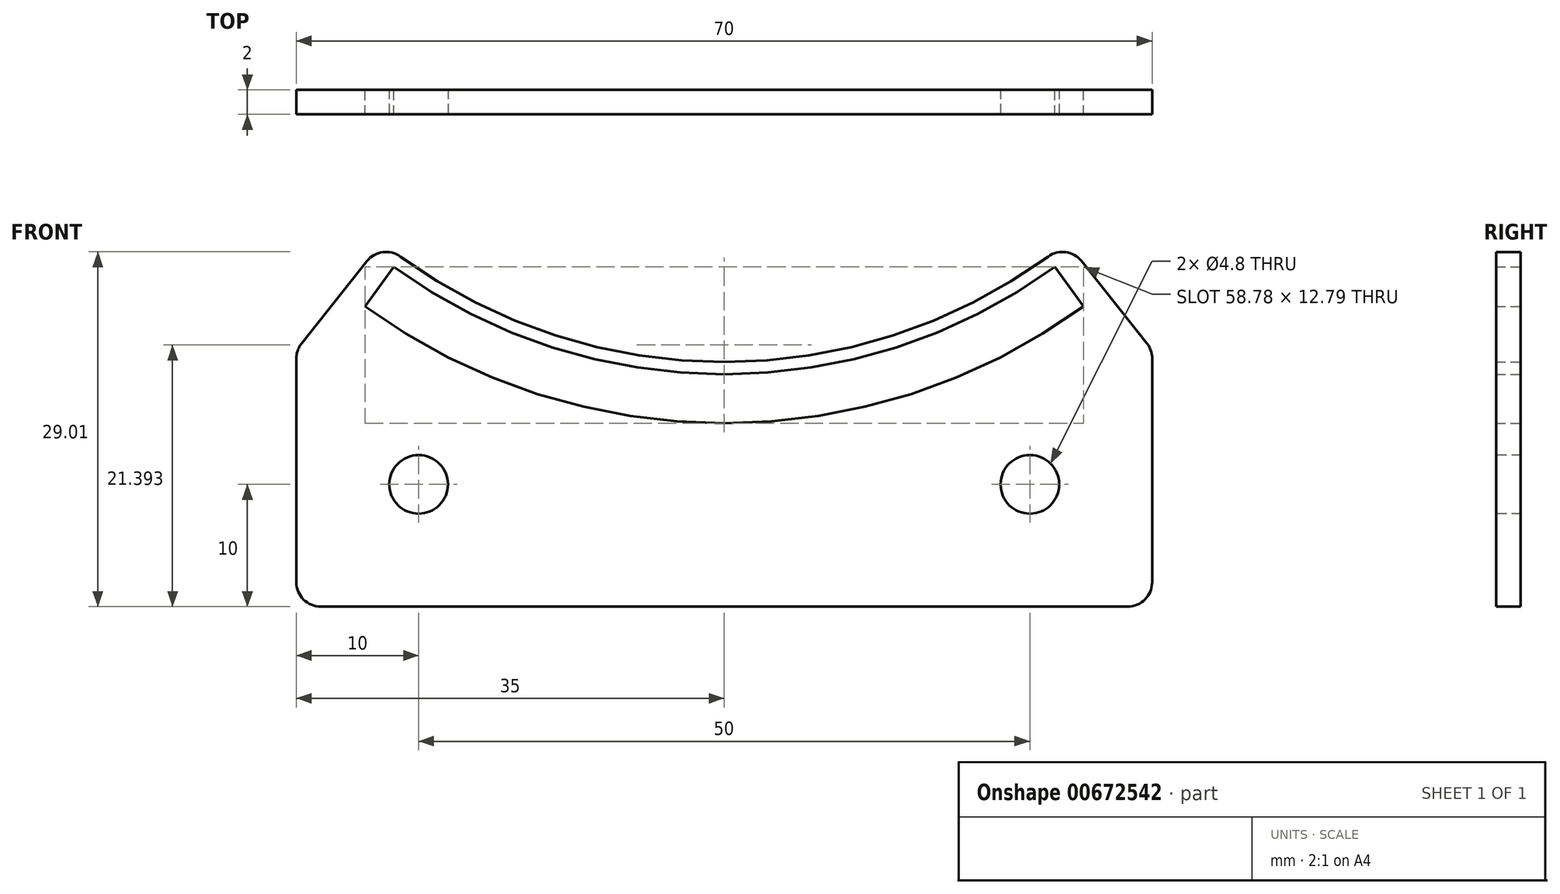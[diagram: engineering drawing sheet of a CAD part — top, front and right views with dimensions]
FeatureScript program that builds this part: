
annotation { "Feature Type Name" : "Feature", "Feature Type Description" : "" }
export const myFeature = defineFeature(function(context is Context, id is Id, definition is map)
    precondition{}
    {
        {
            var Q0;
            Q0=qCreatedBy(makeId("Front.planeOp"),FACE);
            var sketch = newSketch(context, id + "F0", { "sketchPlane" : qUnion([Q0])});
            skArc(sketch, "E0", {"start": v(-29.39, -40.45) * mm, "mid": v(0, -50) * mm, "end": v(29.39, -40.45) * mm});
            skArc(sketch, "E1", {"start": v(-27.04, -37.21) * mm, "mid": v(0, -46) * mm, "end": v(27.04, -37.21) * mm});
            skLineSegment(sketch, "E2", {"start": v(0, 0) * mm, "end": v(0, -50) * mm});
            skLineSegment(sketch, "E3", {"start": v(27.04, -37.21) * mm, "end": v(29.39, -40.45) * mm});
            skLineSegment(sketch, "E4", {"start": v(-27.04, -37.21) * mm, "end": v(-29.39, -40.45) * mm});
            skArc(sketch, "E5", {"start": v(-28.01, -35.22) * mm, "mid": v(0, -45) * mm, "end": v(28.01, -35.22) * mm});
            skLineSegment(sketch, "E6", {"start": v(28.01, -35.22) * mm, "end": v(35, -44) * mm});
            skLineSegment(sketch, "E7", {"start": v(-28.01, -35.22) * mm, "end": v(-35, -44) * mm});
            skLineSegment(sketch, "E8", {"start": v(-35, -65) * mm, "end": v(35, -65) * mm});
            skLineSegment(sketch, "E9", {"start": v(35, -44) * mm, "end": v(35, -65) * mm});
            skLineSegment(sketch, "E10", {"start": v(-35, -44) * mm, "end": v(-35, -65) * mm});
            skSolve(sketch);
        }
        {
            var Q0;
            {var subQ4=sQuery(id+"F0.wireOp",EDGE,"E3");Q0=makeQuery(id+"F0.imprint","IMPRINT",FACE,{"disambiguationData":[TD([[makeQuery(id+"F0.imprint","IMPRINT",EDGE,{"derivedFrom":subQ4}),1.0]])]});}
            extrude(context, id + "F1", {"entities" : qUnion([Q0]), "endBound" : BoundingType.SYMMETRIC, "depth" : 2 * mm, "offsetDistance" : 25 * mm});
        }
        {
            var Q0;
            Q0=makeQuery(id+"F1.opExtrude","SWEPT_EDGE",EDGE,{"disambiguationData":[OSD([sQuery(id+"F0.wireOp",EDGE,"E5"),sQuery(id+"F0.wireOp",EDGE,"E6")])]});
            var Q1;
            Q1=makeQuery(id+"F1.opExtrude","SWEPT_EDGE",EDGE,{"disambiguationData":[OSD([sQuery(id+"F0.wireOp",EDGE,"E6"),sQuery(id+"F0.wireOp",EDGE,"E9")])]});
            var Q2;
            Q2=makeQuery(id+"F1.opExtrude","SWEPT_EDGE",EDGE,{"disambiguationData":[OSD([sQuery(id+"F0.wireOp",EDGE,"E5"),sQuery(id+"F0.wireOp",EDGE,"E7")])]});
            var Q3;
            Q3=makeQuery(id+"F1.opExtrude","SWEPT_EDGE",EDGE,{"disambiguationData":[OSD([sQuery(id+"F0.wireOp",EDGE,"E7"),sQuery(id+"F0.wireOp",EDGE,"E10")])]});
            fillet(context, id + "F2", {"entities" : qUnion([Q0, Q1, Q2, Q3]), "radius" : 2 * mm, "tangentPropagation" : true, "allowEdgeOverflow" : false});
        }
        {
            var Q0;
            Q0=makeQuery(id+"F1.opExtrude","CAP_FACE",FACE,{"disambiguationData":[OSD([sQuery(id+"F0.wireOp",EDGE,"E0"),sQuery(id+"F0.wireOp",EDGE,"E1"),sQuery(id+"F0.wireOp",EDGE,"E3"),sQuery(id+"F0.wireOp",EDGE,"E4"),sQuery(id+"F0.wireOp",EDGE,"E5"),sQuery(id+"F0.wireOp",EDGE,"E6"),sQuery(id+"F0.wireOp",EDGE,"E7"),sQuery(id+"F0.wireOp",EDGE,"E8"),sQuery(id+"F0.wireOp",EDGE,"E9"),sQuery(id+"F0.wireOp",EDGE,"E10")])],"isStart":false});
            var sketch = newSketch(context, id + "F3", { "sketchPlane" : qUnion([Q0])});
            skCircle(sketch, "E11", {"center": v(-25, -55) * mm, "radius": 2.4 * mm});
            skCircle(sketch, "E12", {"center": v(25, -55) * mm, "radius": 2.4 * mm});
            skSolve(sketch);
        }
        {
            var Q0;
            Q0=makeQuery(id+"F3.imprint","IMPRINT",FACE,{"disambiguationData":[TD([[makeQuery(id+"F3.imprint","IMPRINT",EDGE,{"derivedFrom":sQuery(id+"F3.wireOp",EDGE,"E11")}),1.0]])]});
            var Q1;
            Q1=makeQuery(id+"F3.imprint","IMPRINT",FACE,{"disambiguationData":[TD([[makeQuery(id+"F3.imprint","IMPRINT",EDGE,{"derivedFrom":sQuery(id+"F3.wireOp",EDGE,"E12")}),1.0]])]});
            extrude(context, id + "F4", {"entities" : qUnion([Q0, Q1]), "operationType" : NewBodyOperationType.REMOVE, "oppositeDirection" : true, "depth" : 25 * mm, "offsetDistance" : 25 * mm});
        }
        {
            var Q0;
            Q0=makeQuery(id+"F1.opExtrude","SWEPT_EDGE",EDGE,{"disambiguationData":[OSD([sQuery(id+"F0.wireOp",EDGE,"E8"),sQuery(id+"F0.wireOp",EDGE,"E9")])]});
            var Q1;
            Q1=makeQuery(id+"F1.opExtrude","SWEPT_EDGE",EDGE,{"disambiguationData":[OSD([sQuery(id+"F0.wireOp",EDGE,"E8"),sQuery(id+"F0.wireOp",EDGE,"E10")])]});
            fillet(context, id + "F5", {"entities" : qUnion([Q0, Q1]), "radius" : 2 * mm, "tangentPropagation" : true, "allowEdgeOverflow" : false});
        }
    });
